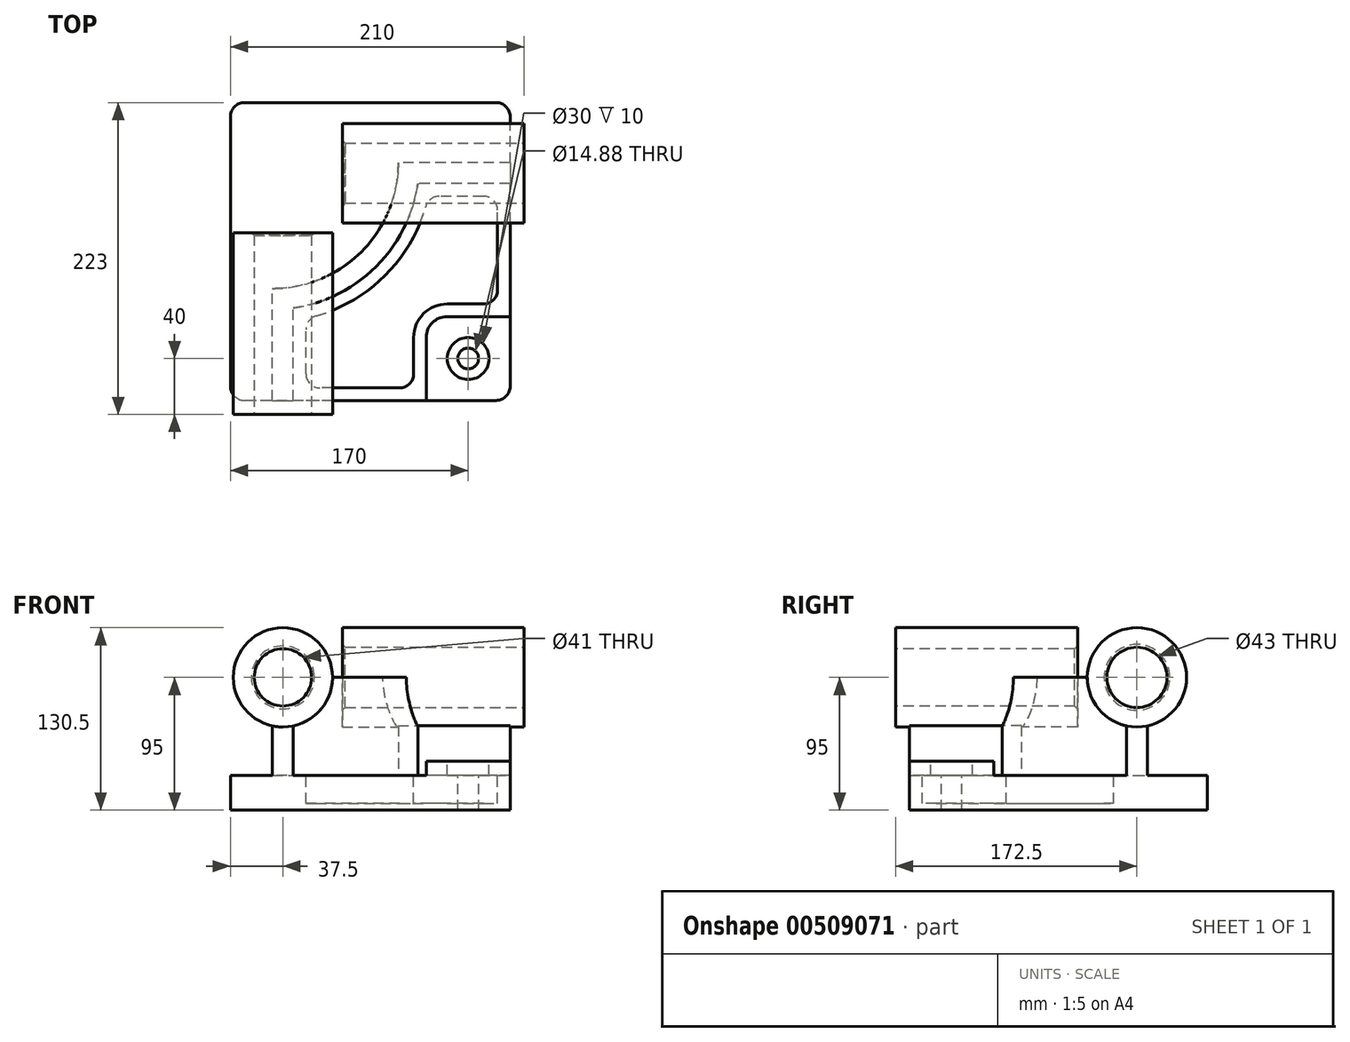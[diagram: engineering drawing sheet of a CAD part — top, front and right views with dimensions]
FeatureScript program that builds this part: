
annotation { "Feature Type Name" : "Feature", "Feature Type Description" : "" }
export const myFeature = defineFeature(function(context is Context, id is Id, definition is map)
    precondition{}
    {
        {
            var Q0;
            Q0=qCreatedBy(makeId("Top.planeOp"),FACE);
            var sketch = newSketch(context, id + "F0", { "sketchPlane" : qUnion([Q0])});
            skLineSegment(sketch, "E0.bottom", {"start": v(-10, 0) * mm, "end": v(-190, 0) * mm});
            skLineSegment(sketch, "E0.top", {"start": v(-10, 213) * mm, "end": v(-190, 213) * mm});
            skLineSegment(sketch, "E0.left", {"start": v(0, 10) * mm, "end": v(0, 203) * mm});
            skLineSegment(sketch, "E0.right", {"start": v(-200, 10) * mm, "end": v(-200, 203) * mm});
            skPoint(sketch, "E1.visualSharp", {"position": v(-200, 213) * mm});
            skArc(sketch, "E1.filletArc", {"start": v(-190, 213) * mm, "mid": v(-197.07, 210.07) * mm, "end": v(-200, 203) * mm});
            skPoint(sketch, "E2.visualSharp", {"position": v(0, 213) * mm});
            skArc(sketch, "E2.filletArc", {"start": v(0, 203) * mm, "mid": v(-2.93, 210.07) * mm, "end": v(-10, 213) * mm});
            skPoint(sketch, "E3.visualSharp", {"position": v(0, 0) * mm});
            skArc(sketch, "E3.filletArc", {"start": v(-10, 0) * mm, "mid": v(-2.93, 2.93) * mm, "end": v(0, 10) * mm});
            skPoint(sketch, "E4.visualSharp", {"position": v(-200, 0) * mm});
            skArc(sketch, "E4.filletArc", {"start": v(-200, 10) * mm, "mid": v(-197.07, 2.93) * mm, "end": v(-190, 0) * mm});
            skSolve(sketch);
        }
        {
            var Q0;
            Q0 = qSketchRegion(id + "F0", true);
            extrude(context, id + "F1", {"entities" : qUnion([Q0]), "depth" : 25 * mm});
        }
        {
            var Q0;
            Q0=makeQuery(id+"F1.opExtrude","CAP_FACE",FACE,{"disambiguationData":[OSD([sQuery(id+"F0.wireOp",EDGE,"E0.bottom"),sQuery(id+"F0.wireOp",EDGE,"E0.top"),sQuery(id+"F0.wireOp",EDGE,"E0.left"),sQuery(id+"F0.wireOp",EDGE,"E0.right"),sQuery(id+"F0.wireOp",EDGE,"E1.filletArc"),sQuery(id+"F0.wireOp",EDGE,"E2.filletArc"),sQuery(id+"F0.wireOp",EDGE,"E3.filletArc"),sQuery(id+"F0.wireOp",EDGE,"E4.filletArc")])],"isStart":false});
            var sketch = newSketch(context, id + "F2", { "sketchPlane" : qUnion([Q0])});
            skLineSegment(sketch, "E5", {"start": v(0, 170) * mm, "end": v(-80, 170) * mm});
            skLineSegment(sketch, "E6", {"start": v(-170, 0) * mm, "end": v(-170, 80) * mm});
            skLineSegment(sketch, "E7.0", {"start": v(0, 155) * mm, "end": v(-66.08, 155) * mm});
            skLineSegment(sketch, "E8.0", {"start": v(-155, 0) * mm, "end": v(-155, 66.08) * mm});
            skLineSegment(sketch, "E9", {"start": v(0, 155) * mm, "end": v(0, 170) * mm});
            skLineSegment(sketch, "E10", {"start": v(-170, 0) * mm, "end": v(-155, 0) * mm});
            skLineSegment(sketch, "E11", {"start": v(-170, 80) * mm, "end": v(-170, 170) * mm, "construction": true});
            skLineSegment(sketch, "E12", {"start": v(-170, 170) * mm, "end": v(-80, 170) * mm, "construction": true});
            skArc(sketch, "E13", {"start": v(-170, 80) * mm, "mid": v(-106.36, 106.36) * mm, "end": v(-80, 170) * mm});
            skArc(sketch, "E14", {"start": v(-155, 66.08) * mm, "mid": v(-95.75, 95.75) * mm, "end": v(-66.08, 155) * mm});
            skSolve(sketch);
        }
        {
            var Q0;
            Q0 = qSketchRegion(id + "F2", true);
            extrude(context, id + "F3", {"entities" : qUnion([Q0]), "operationType" : NewBodyOperationType.ADD, "depth" : 70 * mm});
        }
        {
            var Q0;
            {var subQ0=sQuery(id+"F0.wireOp",EDGE,"E3.filletArc");var subQ1=sQuery(id+"F0.wireOp",EDGE,"E0.left");var subQ2=sQuery(id+"F0.wireOp",EDGE,"E0.bottom");Q0=makeQuery(id+"F3.boolean.opBoolean","SPLIT",FACE,{"disambiguationData":[TD([makeQuery(id+"F1.opExtrude","SWEPT_FACE",FACE,{"disambiguationData":[OSD([subQ0])]})])],"derivedFrom":makeQuery(id+"F1.opExtrude","CAP_FACE",FACE,{"disambiguationData":[OSD([subQ2,sQuery(id+"F0.wireOp",EDGE,"E0.top"),subQ1,sQuery(id+"F0.wireOp",EDGE,"E0.right"),sQuery(id+"F0.wireOp",EDGE,"E1.filletArc"),sQuery(id+"F0.wireOp",EDGE,"E2.filletArc"),subQ0,sQuery(id+"F0.wireOp",EDGE,"E4.filletArc")])],"isStart":false})});}
            var sketch = newSketch(context, id + "F4", { "sketchPlane" : qUnion([Q0])});
            skLineSegment(sketch, "E15.bottom", {"start": v(-45, 60) * mm, "end": v(0, 60) * mm});
            skLineSegment(sketch, "E15.top", {"start": v(-60, 0) * mm, "end": v(-10, 0) * mm});
            skLineSegment(sketch, "E15.left", {"start": v(-60, 45) * mm, "end": v(-60, 0) * mm});
            skLineSegment(sketch, "E15.right", {"start": v(0, 60) * mm, "end": v(0, 10) * mm});
            skPoint(sketch, "E16.visualSharp", {"position": v(0, 0) * mm});
            skArc(sketch, "E16.filletArc", {"start": v(-10, 0) * mm, "mid": v(-2.93, 2.93) * mm, "end": v(0, 10) * mm});
            skPoint(sketch, "E17.visualSharp", {"position": v(-60, 60) * mm});
            skArc(sketch, "E17.filletArc", {"start": v(-45, 60) * mm, "mid": v(-55.6, 55.6) * mm, "end": v(-60, 45) * mm});
            skSolve(sketch);
        }
        {
            var Q0;
            Q0 = qSketchRegion(id + "F4", true);
            extrude(context, id + "F5", {"entities" : qUnion([Q0]), "operationType" : NewBodyOperationType.ADD, "depth" : 10 * mm});
        }
        {
            var Q0;
            Q0=makeQuery(id+"F5.opExtrude","CAP_FACE",FACE,{"disambiguationData":[OSD([sQuery(id+"F4.wireOp",EDGE,"E15.bottom"),sQuery(id+"F4.wireOp",EDGE,"E15.top"),sQuery(id+"F4.wireOp",EDGE,"E15.left"),sQuery(id+"F4.wireOp",EDGE,"E15.right"),sQuery(id+"F4.wireOp",EDGE,"E16.filletArc"),sQuery(id+"F4.wireOp",EDGE,"E17.filletArc")])],"isStart":false});
            var sketch = newSketch(context, id + "F6", { "sketchPlane" : qUnion([Q0])});
            skCircle(sketch, "E18", {"center": v(-30, 30) * mm, "radius": 15 * mm});
            skSolve(sketch);
        }
        {
            var Q0;
            Q0=makeQuery(id+"F6.imprint","IMPRINT",FACE,{"disambiguationData":[TD([[makeQuery(id+"F6.imprint","IMPRINT",EDGE,{"derivedFrom":sQuery(id+"F6.wireOp",EDGE,"E18")}),1.0]])]});
            extrude(context, id + "F7", {"entities" : qUnion([Q0]), "operationType" : NewBodyOperationType.REMOVE, "oppositeDirection" : true, "depth" : 10 * mm, "offsetDistance" : 25 * mm});
        }
        {
            var Q0;
            Q0=makeQuery(id+"F7.boolean.opBoolean","COPY",FACE,{"derivedFrom":makeQuery(id+"F7.opExtrude","CAP_FACE",FACE,{"disambiguationData":[OSD([sQuery(id+"F6.wireOp",EDGE,"E18")])],"isStart":false})});
            var sketch = newSketch(context, id + "F8", { "sketchPlane" : qUnion([Q0])});
            skCircle(sketch, "E19", {"center": v(-30, 30) * mm, "radius": 7.44 * mm});
            skSolve(sketch);
        }
        {
            var Q0;
            Q0 = qSketchRegion(id + "F8", true);
            extrude(context, id + "F9", {"entities" : qUnion([Q0]), "operationType" : NewBodyOperationType.REMOVE, "endBound" : BoundingType.THROUGH_ALL, "oppositeDirection" : true, "depth" : 25 * mm});
        }
        {
            var Q0;
            {var subQ0=sQuery(id+"F0.wireOp",EDGE,"E3.filletArc");var subQ1=sQuery(id+"F0.wireOp",EDGE,"E0.left");var subQ2=sQuery(id+"F0.wireOp",EDGE,"E0.bottom");Q0=makeQuery(id+"F3.boolean.opBoolean","SPLIT",FACE,{"disambiguationData":[TD([makeQuery(id+"F1.opExtrude","SWEPT_FACE",FACE,{"disambiguationData":[OSD([subQ0])]})])],"derivedFrom":makeQuery(id+"F1.opExtrude","CAP_FACE",FACE,{"disambiguationData":[OSD([subQ2,sQuery(id+"F0.wireOp",EDGE,"E0.top"),subQ1,sQuery(id+"F0.wireOp",EDGE,"E0.right"),sQuery(id+"F0.wireOp",EDGE,"E1.filletArc"),sQuery(id+"F0.wireOp",EDGE,"E2.filletArc"),subQ0,sQuery(id+"F0.wireOp",EDGE,"E4.filletArc")])],"isStart":false})});}
            var sketch = newSketch(context, id + "F10", { "sketchPlane" : qUnion([Q0])});
            skArc(sketch, "E20.1", {"start": v(-155, 66.08) * mm, "mid": v(-95.75, 95.75) * mm, "end": v(-66.08, 155) * mm});
            skLineSegment(sketch, "E20.2", {"start": v(0, 155) * mm, "end": v(-66.08, 155) * mm});
            skLineSegment(sketch, "E20.3", {"start": v(0, 60) * mm, "end": v(0, 155) * mm});
            skLineSegment(sketch, "E20.4", {"start": v(-45, 60) * mm, "end": v(0, 60) * mm});
            skArc(sketch, "E20.5", {"start": v(-45, 60) * mm, "mid": v(-55.6, 55.6) * mm, "end": v(-60, 45) * mm});
            skLineSegment(sketch, "E20.6", {"start": v(-60, 45) * mm, "end": v(-60, 0) * mm});
            skLineSegment(sketch, "E20.7", {"start": v(-60, 0) * mm, "end": v(-155, 0) * mm});
            skLineSegment(sketch, "E20.8", {"start": v(-155, 0) * mm, "end": v(-155, 66.08) * mm});
            skLineSegment(sketch, "E21.0", {"start": v(-9, 79) * mm, "end": v(-9, 136) * mm});
            skLineSegment(sketch, "E21.1", {"start": v(-45, 69) * mm, "end": v(-19, 69) * mm});
            skLineSegment(sketch, "E21.2", {"start": v(-19, 146) * mm, "end": v(-50.75, 146) * mm});
            skArc(sketch, "E21.3", {"start": v(-45, 69) * mm, "mid": v(-61.97, 61.97) * mm, "end": v(-69, 45) * mm});
            skArc(sketch, "E21.4", {"start": v(-138.74, 60.37) * mm, "mid": v(-89.39, 89.39) * mm, "end": v(-60.37, 138.74) * mm});
            skLineSegment(sketch, "E21.5", {"start": v(-146, 19) * mm, "end": v(-146, 50.75) * mm});
            skLineSegment(sketch, "E21.6", {"start": v(-79, 9) * mm, "end": v(-136, 9) * mm});
            skLineSegment(sketch, "E21.7", {"start": v(-69, 45) * mm, "end": v(-69, 19) * mm});
            skPoint(sketch, "E22.visualSharp", {"position": v(-9, 146) * mm});
            skArc(sketch, "E22.filletArc", {"start": v(-9, 136) * mm, "mid": v(-11.93, 143.07) * mm, "end": v(-19, 146) * mm});
            skPoint(sketch, "E23.visualSharp", {"position": v(-58.55, 146) * mm});
            skArc(sketch, "E23.filletArc", {"start": v(-50.75, 146) * mm, "mid": v(-56.78, 143.98) * mm, "end": v(-60.37, 138.74) * mm});
            skPoint(sketch, "E24.visualSharp", {"position": v(-146, 58.55) * mm});
            skArc(sketch, "E24.filletArc", {"start": v(-138.74, 60.37) * mm, "mid": v(-143.98, 56.78) * mm, "end": v(-146, 50.75) * mm});
            skPoint(sketch, "E25.visualSharp", {"position": v(-146, 9) * mm});
            skArc(sketch, "E25.filletArc", {"start": v(-146, 19) * mm, "mid": v(-143.07, 11.93) * mm, "end": v(-136, 9) * mm});
            skPoint(sketch, "E26.visualSharp", {"position": v(-69, 9) * mm});
            skArc(sketch, "E26.filletArc", {"start": v(-79, 9) * mm, "mid": v(-71.93, 11.93) * mm, "end": v(-69, 19) * mm});
            skPoint(sketch, "E27.visualSharp", {"position": v(-9, 69) * mm});
            skArc(sketch, "E27.filletArc", {"start": v(-19, 69) * mm, "mid": v(-11.93, 71.93) * mm, "end": v(-9, 79) * mm});
            skSolve(sketch);
        }
        {
            var Q0;
            Q0=makeQuery(id+"F10.imprint","IMPRINT",FACE,{"disambiguationData":[TD([[makeQuery(id+"F10.imprint","IMPRINT",EDGE,{"derivedFrom":sQuery(id+"F10.wireOp",EDGE,"E21.0")}),1.0]])]});
            extrude(context, id + "F11", {"entities" : qUnion([Q0]), "operationType" : NewBodyOperationType.REMOVE, "oppositeDirection" : true, "depth" : 20 * mm});
        }
        {
            var Q0;
            Q0=makeQuery(id+"F5.boolean.opBoolean","MERGE",FACE,{"derivedFrom":[makeQuery(id+"F3.boolean.opBoolean","MERGE",FACE,{"derivedFrom":[makeQuery(id+"F1.opExtrude","SWEPT_FACE",FACE,{"disambiguationData":[OSD([sQuery(id+"F0.wireOp",EDGE,"E0.bottom")])]}),makeQuery(id+"F3.opExtrude","SWEPT_FACE",FACE,{"disambiguationData":[OSD([sQuery(id+"F2.wireOp",EDGE,"E10")])]})]}),makeQuery(id+"F5.opExtrude","SWEPT_FACE",FACE,{"disambiguationData":[OSD([sQuery(id+"F4.wireOp",EDGE,"E15.top")])]})]});
            cPlane(context, id + "F12", {"entities" : qUnion([Q0]), "cplaneType" : CPlaneType.OFFSET, "offset" : 10 * mm, "width" : 150 * mm, "height" : 150 * mm});
        }
        {
            var Q0;
            Q0=qCreatedBy(id+"F12.planeOp",FACE);
            var sketch = newSketch(context, id + "F13", { "sketchPlane" : qUnion([Q0])});
            skCircle(sketch, "E28", {"center": v(-162.5, 95) * mm, "radius": 35.5 * mm});
            skSolve(sketch);
        }
        {
            var Q0;
            Q0 = qSketchRegion(id + "F13", true);
            extrude(context, id + "F14", {"entities" : qUnion([Q0]), "operationType" : NewBodyOperationType.ADD, "oppositeDirection" : true, "depth" : 130 * mm});
        }
        {
            var Q0;
            Q0=makeQuery(id+"F14.opExtrude","CAP_FACE",FACE,{"disambiguationData":[OSD([sQuery(id+"F13.wireOp",EDGE,"E28")])],"isStart":true});
            var sketch = newSketch(context, id + "F15", { "sketchPlane" : qUnion([Q0])});
            skCircle(sketch, "E29", {"center": v(-162.5, 95) * mm, "radius": 20.5 * mm});
            skSolve(sketch);
        }
        {
            var Q0;
            Q0 = qSketchRegion(id + "F15", true);
            extrude(context, id + "F16", {"entities" : qUnion([Q0]), "operationType" : NewBodyOperationType.REMOVE, "endBound" : BoundingType.THROUGH_ALL, "oppositeDirection" : true, "depth" : 25 * mm});
        }
        {
            var Q0;
            Q0=makeQuery(id+"F5.boolean.opBoolean","MERGE",FACE,{"derivedFrom":[makeQuery(id+"F3.boolean.opBoolean","MERGE",FACE,{"derivedFrom":[makeQuery(id+"F1.opExtrude","SWEPT_FACE",FACE,{"disambiguationData":[OSD([sQuery(id+"F0.wireOp",EDGE,"E0.left")])]}),makeQuery(id+"F3.opExtrude","SWEPT_FACE",FACE,{"disambiguationData":[OSD([sQuery(id+"F2.wireOp",EDGE,"E9")])]})]}),makeQuery(id+"F5.opExtrude","SWEPT_FACE",FACE,{"disambiguationData":[OSD([sQuery(id+"F4.wireOp",EDGE,"E15.right")])]})]});
            cPlane(context, id + "F17", {"entities" : qUnion([Q0]), "cplaneType" : CPlaneType.OFFSET, "offset" : 10 * mm, "width" : 150 * mm, "height" : 150 * mm});
        }
        {
            var Q0;
            Q0=qCreatedBy(id+"F17.planeOp",FACE);
            var sketch = newSketch(context, id + "F18", { "sketchPlane" : qUnion([Q0])});
            skCircle(sketch, "E30", {"center": v(162.5, 95) * mm, "radius": 35.5 * mm});
            skSolve(sketch);
        }
        {
            var Q0;
            Q0 = qSketchRegion(id + "F18", true);
            extrude(context, id + "F19", {"entities" : qUnion([Q0]), "operationType" : NewBodyOperationType.ADD, "oppositeDirection" : true, "depth" : 130 * mm});
        }
        {
            var Q0;
            Q0=makeQuery(id+"F19.opExtrude","CAP_FACE",FACE,{"disambiguationData":[OSD([sQuery(id+"F18.wireOp",EDGE,"E30")])],"isStart":true});
            var sketch = newSketch(context, id + "F20", { "sketchPlane" : qUnion([Q0])});
            skCircle(sketch, "E31", {"center": v(162.5, 95) * mm, "radius": 21.5 * mm});
            skSolve(sketch);
        }
        {
            var Q0;
            Q0 = qSketchRegion(id + "F20", true);
            extrude(context, id + "F21", {"entities" : qUnion([Q0]), "operationType" : NewBodyOperationType.REMOVE, "endBound" : BoundingType.THROUGH_ALL, "oppositeDirection" : true, "depth" : 25 * mm});
        }
        {
            var Q0;
            Q0=makeQuery(id+"F16.boolean.opBoolean","COPY",EDGE,{"derivedFrom":makeQuery(id+"F16.opExtrude","CAP_EDGE",EDGE,{"disambiguationData":[OSD([sQuery(id+"F15.wireOp",EDGE,"E29")])],"isStart":true})});
            var Q1;
            Q1=makeQuery(id+"F16.boolean.opBoolean","INTERSECT",EDGE,{"derivedFrom":[makeQuery(id+"F14.opExtrude","CAP_FACE",FACE,{"disambiguationData":[OSD([sQuery(id+"F13.wireOp",EDGE,"E28")])],"isStart":false}),makeQuery(id+"F16.opExtrude","SWEPT_FACE",FACE,{"disambiguationData":[OSD([sQuery(id+"F15.wireOp",EDGE,"E29")])]})]});
            var Q2;
            Q2=makeQuery(id+"F21.boolean.opBoolean","COPY",EDGE,{"derivedFrom":makeQuery(id+"F21.opExtrude","CAP_EDGE",EDGE,{"disambiguationData":[OSD([sQuery(id+"F20.wireOp",EDGE,"E31")])],"isStart":true})});
            var Q3;
            Q3=makeQuery(id+"F21.boolean.opBoolean","INTERSECT",EDGE,{"derivedFrom":[makeQuery(id+"F19.opExtrude","CAP_FACE",FACE,{"disambiguationData":[OSD([sQuery(id+"F18.wireOp",EDGE,"E30")])],"isStart":false}),makeQuery(id+"F21.opExtrude","SWEPT_FACE",FACE,{"disambiguationData":[OSD([sQuery(id+"F20.wireOp",EDGE,"E31")])]})]});
            chamfer(context, id + "F22", {"entities" : qUnion([Q0, Q1, Q2, Q3]), "chamferType" : ChamferType.OFFSET_ANGLE, "width" : 2 * mm, "oppositeDirection" : false, "angle" : 45 * degree, "tangentPropagation" : true});
        }
    });
